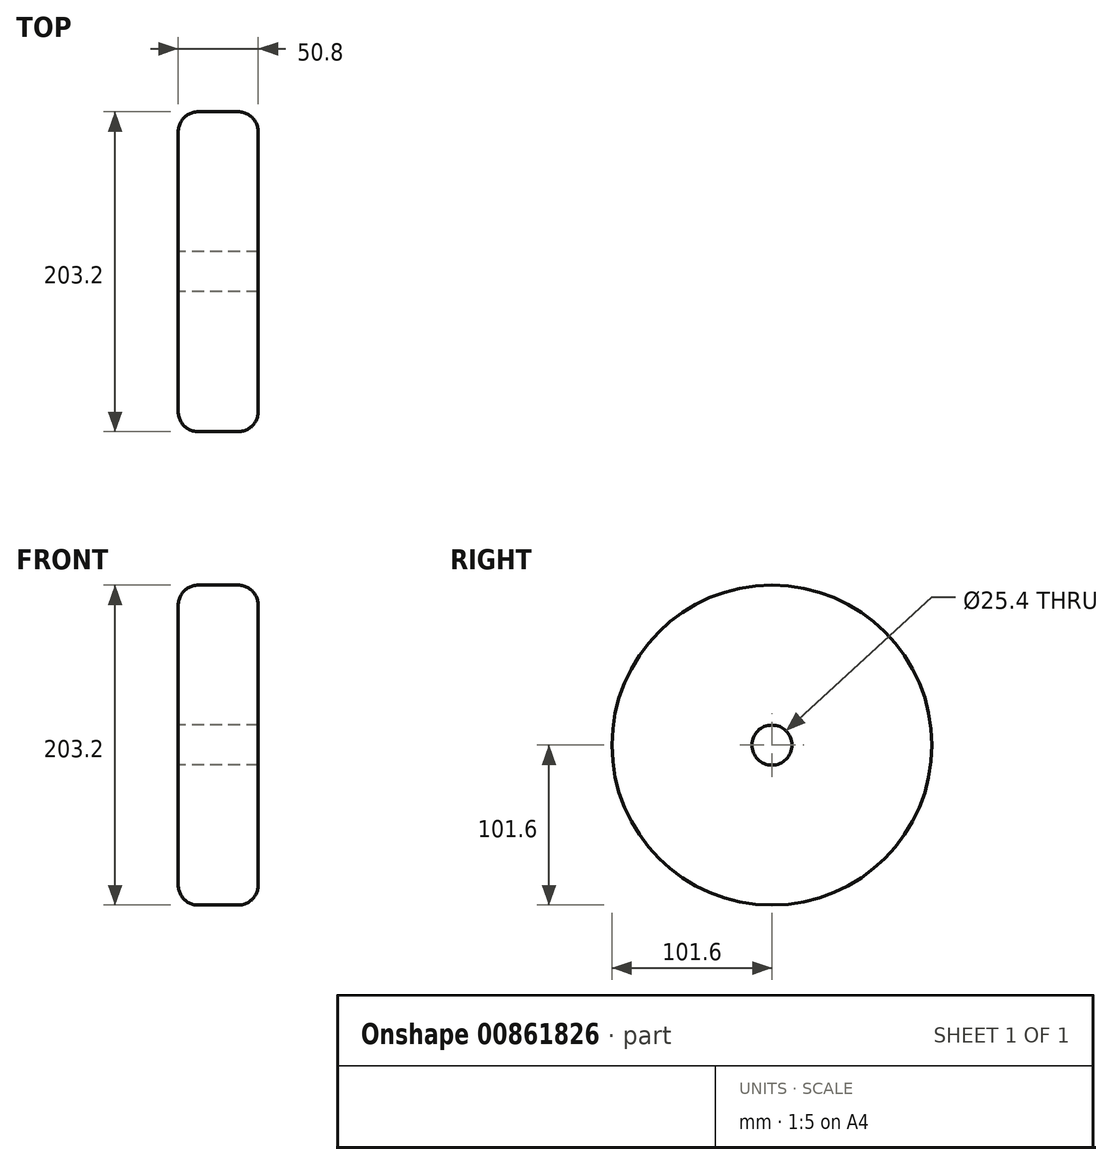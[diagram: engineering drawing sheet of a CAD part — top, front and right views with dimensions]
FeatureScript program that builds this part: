
annotation { "Feature Type Name" : "Feature", "Feature Type Description" : "" }
export const myFeature = defineFeature(function(context is Context, id is Id, definition is map)
    precondition{}
    {
        {
            var Q0;
            Q0=qCreatedBy(makeId("Right.planeOp"),FACE);
            var sketch = newSketch(context, id + "F0", { "sketchPlane" : qUnion([Q0])});
            skCircle(sketch, "E0", {"center": v(0, 0) * mm, "radius": 101.6 * mm});
            skSolve(sketch);
        }
        {
            var Q0;
            Q0 = qSketchRegion(id + "F0", true);
            extrude(context, id + "F1", {"entities" : qUnion([Q0]), "depth" : 50.8 * mm, "offsetDistance" : 25.4 * mm, "symmetric" : true});
        }
        {
            var Q0;
            Q0=makeQuery(id+"F1.opExtrude","CAP_EDGE",EDGE,{"disambiguationData":[OSD([sQuery(id+"F0.wireOp",EDGE,"E0")])],"isStart":true});
            var Q1;
            Q1=makeQuery(id+"F1.opExtrude","CAP_EDGE",EDGE,{"disambiguationData":[OSD([sQuery(id+"F0.wireOp",EDGE,"E0")])],"isStart":false});
            fillet(context, id + "F2", {"entities" : qUnion([Q0, Q1]), "radius" : 12.7 * mm, "tangentPropagation" : true, "allowEdgeOverflow" : false});
        }
        {
            var Q0;
            Q0=makeQuery(id+"F1.opExtrude","CAP_FACE",FACE,{"disambiguationData":[OSD([sQuery(id+"F0.wireOp",EDGE,"E0")])],"isStart":true});
            var sketch = newSketch(context, id + "F3", { "sketchPlane" : qUnion([Q0])});
            skCircle(sketch, "E1", {"center": v(0, 0) * mm, "radius": 12.7 * mm});
            skSolve(sketch);
        }
        {
            var Q0;
            Q0 = qSketchRegion(id + "F3", true);
            extrude(context, id + "F4", {"entities" : qUnion([Q0]), "operationType" : NewBodyOperationType.REMOVE, "endBound" : BoundingType.THROUGH_ALL, "oppositeDirection" : true, "depth" : 25.4 * mm, "offsetDistance" : 25.4 * mm});
        }
    });
